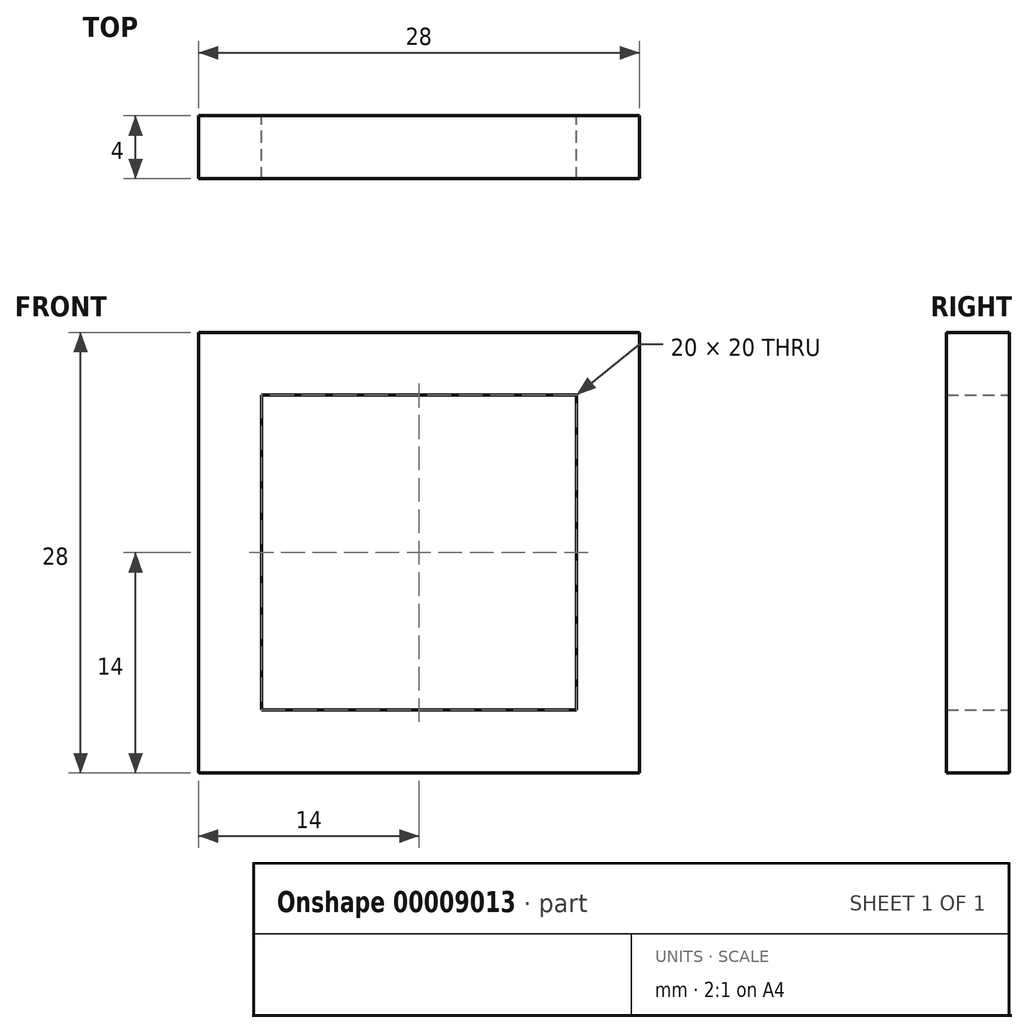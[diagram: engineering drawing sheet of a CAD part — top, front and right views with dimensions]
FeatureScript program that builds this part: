
annotation { "Feature Type Name" : "Feature", "Feature Type Description" : "" }
export const myFeature = defineFeature(function(context is Context, id is Id, definition is map)
    precondition{}
    {
        {
            var Q0;
            Q0=qCreatedBy(makeId("Front.planeOp"),FACE);
            var sketch = newSketch(context, id + "F0", { "sketchPlane" : qUnion([Q0])});
            skLineSegment(sketch, "E0.rect.bottom", {"start": v(10, -10) * mm, "end": v(-10, -10) * mm});
            skLineSegment(sketch, "E0.rect.top", {"start": v(10, 10) * mm, "end": v(-10, 10) * mm});
            skLineSegment(sketch, "E0.rect.left", {"start": v(10, -10) * mm, "end": v(10, 10) * mm});
            skLineSegment(sketch, "E0.rect.right", {"start": v(-10, -10) * mm, "end": v(-10, 10) * mm});
            skPoint(sketch, "E0.rect.middle", {"position": v(0, 0) * mm});
            skLineSegment(sketch, "E1.0", {"start": v(14, 14) * mm, "end": v(-14, 14) * mm});
            skLineSegment(sketch, "E1.1", {"start": v(14, -14) * mm, "end": v(14, 14) * mm});
            skLineSegment(sketch, "E1.2", {"start": v(14, -14) * mm, "end": v(-14, -14) * mm});
            skLineSegment(sketch, "E1.3", {"start": v(-14, -14) * mm, "end": v(-14, 14) * mm});
            skSolve(sketch);
        }
        {
            var Q0;
            Q0=makeQuery(id+"F0.imprint","IMPRINT",FACE,{"disambiguationData":[TD([[makeQuery(id+"F0.imprint","IMPRINT",EDGE,{"derivedFrom":sQuery(id+"F0.wireOp",EDGE,"E0.rect.bottom")}),1.0]])]});
            extrude(context, id + "F1", {"entities" : qUnion([Q0]), "depth" : 4 * mm});
        }
    });
